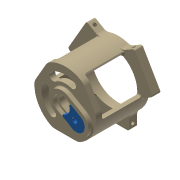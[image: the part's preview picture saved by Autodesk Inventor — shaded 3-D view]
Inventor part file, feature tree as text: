
AUTODESK INVENTOR PART (.ipt)
format: ipt  version: 2015 (Build 190159000, 159)  size: 2,890,752 bytes
history: native  units: in
note: dims shown in document units (in); Inventor stores cm internally (conversion verified against a paired STEP export)
features: extrude x13, sketch x11, fillet x8, other x6, projected_geometry x5, pattern_circular x4, plane x3, mirror x1
ambient origin geometry x8: Origin, YZ Plane, XZ Plane, XY Plane, X Axis, Y Axis, Z Axis, Center Point
bodies: Body1 (feature_tree), Body2 (feature_tree), Body3 (feature_tree), Body4 (feature_tree), Body5 (feature_tree), Body6 (feature_tree), Body7 (feature_tree), Body8 (feature_tree), Body9 (feature_tree), Body10 (feature_tree), Body11 (feature_tree), Body12 (feature_tree), Body13 (feature_tree), Body14 (feature_tree), Body15 (feature_tree), Body16 (feature_tree), Body17 (feature_tree), Body18 (feature_tree), Body19 (feature_tree), Body20 (feature_tree), Body21 (feature_tree), Body22 (feature_tree), Body23 (feature_tree), Body24 (feature_tree), Body25 (feature_tree), Body26 (feature_tree), Body27 (feature_tree), Body28 (feature_tree), Body29 (feature_tree), Body30 (feature_tree), Body31 (feature_tree), Body32 (feature_tree), Body33 (feature_tree), Body34 (feature_tree), Body35 (feature_tree), Body36 (feature_tree), Body37 (feature_tree), Body38 (feature_tree), Body39 (feature_tree), Body40 (feature_tree), Body41 (feature_tree), Body42 (feature_tree), Body43 (feature_tree), Body44 (feature_tree), Body45 (feature_tree), Body46 (feature_tree), Body47 (feature_tree), Body48 (feature_tree), Body49 (feature_tree), Body50 (feature_tree), Body51 (feature_tree), Body52 (feature_tree), Body53 (feature_tree), Body54 (feature_tree), Body55 (feature_tree), Body56 (feature_tree), Body57 (feature_tree), Body58 (feature_tree), Body59 (feature_tree), Body60 (feature_tree), Body61 (feature_tree), Body62 (feature_tree), Body63 (feature_tree), Body64 (feature_tree), Body65 (feature_tree), Body66 (feature_tree), Body67 (feature_tree), Body68 (feature_tree), Body69 (feature_tree), Body70 (feature_tree), Body71 (feature_tree), Body72 (feature_tree), Body73 (feature_tree), Body74 (feature_tree), Body75 (feature_tree), Body76 (feature_tree), Body77 (feature_tree), Body78 (feature_tree), Body79 (feature_tree), Body80 (feature_tree), Body81 (feature_tree), Body82 (feature_tree), Body83 (feature_tree), Body84 (feature_tree), Body85 (feature_tree), Body86 (feature_tree), Body87 (feature_tree), Body88 (feature_tree), Body89 (feature_tree), Body90 (feature_tree), Body91 (feature_tree), Body92 (feature_tree), Body93 (feature_tree), Body94 (feature_tree), Body95 (feature_tree), Body96 (feature_tree), Body97 (feature_tree), Body98 (feature_tree), Body99 (feature_tree), Body100 (feature_tree), Body101 (feature_tree), Body102 (feature_tree), Body103 (feature_tree), Body104 (feature_tree), Body105 (feature_tree), Body106 (feature_tree), Body107 (feature_tree), Body108 (feature_tree), Body109 (feature_tree), Body110 (feature_tree), Body111 (feature_tree), Body112 (feature_tree), Body113 (feature_tree), Body114 (feature_tree), Body115 (feature_tree), Body116 (feature_tree), Body117 (feature_tree), Body118 (feature_tree), Body119 (feature_tree), Body120 (feature_tree), Body121 (feature_tree), Body122 (feature_tree), Body123 (feature_tree), Body124 (feature_tree), Body125 (feature_tree), Body126 (feature_tree), Body127 (feature_tree), Body128 (feature_tree), Body129 (feature_tree), Body130 (feature_tree), Body131 (feature_tree), Body132 (feature_tree), Body133 (feature_tree), Body134 (feature_tree), Body135 (feature_tree), Body136 (feature_tree), Body137 (feature_tree), Body138 (feature_tree), Body139 (feature_tree), Body140 (feature_tree), Body141 (feature_tree), Body142 (feature_tree), Body143 (feature_tree), Body144 (feature_tree), Body145 (feature_tree), Body146 (feature_tree), Body147 (feature_tree), Body148 (feature_tree), Body149 (feature_tree), Body150 (feature_tree), Body151 (feature_tree), Body152 (feature_tree), Body153 (feature_tree), Body154 (feature_tree), Body155 (feature_tree), Body156 (feature_tree), Body157 (feature_tree), Body158 (feature_tree), Body159 (feature_tree), Body160 (feature_tree), Body161 (feature_tree), Body162 (feature_tree), Body163 (feature_tree), Body164 (feature_tree), Body165 (feature_tree), Body166 (feature_tree), Body167 (feature_tree), Body168 (feature_tree), Body169 (feature_tree), Body170 (feature_tree), Body171 (feature_tree), Body172 (feature_tree), Body173 (feature_tree), Body174 (feature_tree), Body175 (feature_tree), Body176 (feature_tree), Body177 (feature_tree), Body178 (feature_tree), Body179 (feature_tree), Body180 (feature_tree), Body181 (feature_tree), Body182 (feature_tree), Body183 (feature_tree), Body184 (feature_tree), Body185 (feature_tree), Body186 (feature_tree), Body187 (feature_tree), Body188 (feature_tree), Body189 (feature_tree), Body190 (feature_tree), Body191 (feature_tree), Body192 (feature_tree), Body193 (feature_tree), Body194 (feature_tree), Body195 (feature_tree), Body196 (feature_tree), Body197 (feature_tree), Body198 (feature_tree), Body199 (feature_tree), Body200 (feature_tree), Body201 (feature_tree), Body202 (feature_tree), Body203 (feature_tree), Body204 (feature_tree), Body205 (feature_tree), Body206 (feature_tree), Body207 (feature_tree), Body208 (feature_tree), Body209 (feature_tree), Body210 (feature_tree), Body211 (feature_tree), Body212 (feature_tree), Body213 (feature_tree), Body214 (feature_tree), Body215 (feature_tree), Body216 (feature_tree), Body217 (feature_tree), Body218 (feature_tree), Body219 (feature_tree), Body220 (feature_tree), Body221 (feature_tree), Body222 (feature_tree), Body223 (feature_tree), Body224 (feature_tree), Body225 (feature_tree), Body226 (feature_tree), Body227 (feature_tree), Body228 (feature_tree), Body229 (feature_tree), Body230 (feature_tree), Body231 (feature_tree), Body232 (feature_tree), Body233 (feature_tree), Body234 (feature_tree), Body235 (feature_tree), Body236 (feature_tree), Body237 (feature_tree), Body238 (feature_tree), Body239 (feature_tree), Body240 (feature_tree), Body241 (feature_tree), Body242 (feature_tree), Body243 (feature_tree), Body244 (feature_tree), Body245 (feature_tree), Body246 (feature_tree), Body247 (feature_tree), Body248 (feature_tree), Body249 (feature_tree), Body250 (feature_tree), Body251 (feature_tree), Body252 (feature_tree), Body253 (feature_tree), Body254 (feature_tree), Body255 (feature_tree), Body256 (feature_tree), Body257 (feature_tree), Body258 (feature_tree), Body259 (feature_tree), Body260 (feature_tree), Body261 (feature_tree), Body262 (feature_tree), Body263 (feature_tree), Body264 (feature_tree), Body265 (feature_tree), Body266 (feature_tree), Body267 (feature_tree), Body268 (feature_tree), Body269 (feature_tree), Body270 (feature_tree), Body271 (feature_tree), Body272 (feature_tree), Body273 (feature_tree), Body274 (feature_tree), Body275 (feature_tree), Body276 (feature_tree), Body277 (feature_tree), Body278 (feature_tree), Body279 (feature_tree), Body280 (feature_tree), Body281 (feature_tree), Body282 (feature_tree), Body283 (feature_tree), Body284 (feature_tree), Body285 (feature_tree), Body286 (feature_tree), Body287 (feature_tree), Body288 (feature_tree), Body289 (feature_tree), Body290 (feature_tree), Body291 (feature_tree), Body292 (feature_tree), Body293 (feature_tree), Body294 (feature_tree), Body295 (feature_tree), Body296 (feature_tree), Body297 (feature_tree), Body298 (feature_tree), Body299 (feature_tree), Body300 (feature_tree), Body301 (feature_tree), Body302 (feature_tree), Body303 (feature_tree), Body304 (feature_tree), Body305 (feature_tree), Body306 (feature_tree), Body307 (feature_tree), Body308 (feature_tree), Body309 (feature_tree), Body310 (feature_tree), Body311 (feature_tree), Body312 (feature_tree), Body313 (feature_tree), Body314 (feature_tree), Body315 (feature_tree), Body316 (feature_tree), Body317 (feature_tree), Body318 (feature_tree), Body319 (feature_tree), Body320 (feature_tree), Body321 (feature_tree), Body322 (feature_tree), Body323 (feature_tree), Body324 (feature_tree), Body325 (feature_tree), Body326 (feature_tree), Body327 (feature_tree), Body328 (feature_tree), Body329 (feature_tree), Body330 (feature_tree), Body331 (feature_tree), Body332 (feature_tree), Body333 (feature_tree), Body334 (feature_tree), Body335 (feature_tree), Body336 (feature_tree), Body337 (feature_tree), Body338 (feature_tree), Body339 (feature_tree), Body340 (feature_tree), Body341 (feature_tree), Body342 (feature_tree), Body343 (feature_tree), Body344 (feature_tree), Body345 (feature_tree), Body346 (feature_tree), Body347 (feature_tree), Body348 (feature_tree), Body349 (feature_tree), Body350 (feature_tree), Body351 (feature_tree), Body352 (feature_tree), Body353 (feature_tree), Body354 (feature_tree), Body355 (feature_tree), Body356 (feature_tree), Body357 (feature_tree), Body358 (feature_tree), Body359 (feature_tree), Body360 (feature_tree), Body361 (feature_tree), Body362 (feature_tree), Body363 (feature_tree), Body364 (feature_tree), Body365 (feature_tree), Body366 (feature_tree), Body367 (feature_tree), Body368 (feature_tree), Body369 (feature_tree), Body370 (feature_tree), Body371 (feature_tree), Body372 (feature_tree), Body373 (feature_tree), Body374 (feature_tree), Body375 (feature_tree), Body376 (feature_tree), Body377 (feature_tree), Body378 (feature_tree), Body379 (feature_tree), Body380 (feature_tree), Body381 (feature_tree), Body382 (feature_tree), Body383 (feature_tree), Body384 (feature_tree), Body385 (feature_tree), Body386 (feature_tree), Body387 (feature_tree), Body388 (feature_tree), Body389 (feature_tree), Body390 (feature_tree), Body391 (feature_tree), Body392 (feature_tree), Body393 (feature_tree), Body394 (feature_tree), Body395 (feature_tree), Body396 (feature_tree), Body397 (feature_tree), Body398 (feature_tree), Body399 (feature_tree), Body400 (feature_tree), Body401 (feature_tree), Body402 (feature_tree), Body403 (feature_tree), Body404 (feature_tree), Body405 (feature_tree), Body406 (feature_tree), Body407 (feature_tree), Body408 (feature_tree), Body409 (feature_tree), Body410 (feature_tree), Body411 (feature_tree), Body412 (feature_tree), Body413 (feature_tree), Body414 (feature_tree), Body415 (feature_tree), Body416 (feature_tree), Body417 (feature_tree), Body418 (feature_tree), Body419 (feature_tree), Body420 (feature_tree), Body421 (feature_tree), Body422 (feature_tree), Body423 (feature_tree), Body424 (feature_tree), Body425 (feature_tree), Body426 (feature_tree), Body427 (feature_tree), Body428 (feature_tree), Body429 (feature_tree), Body430 (feature_tree), Body431 (feature_tree), Body432 (feature_tree), Body433 (feature_tree), Body434 (feature_tree), Body435 (feature_tree), Body436 (feature_tree), Body437 (feature_tree), Body438 (feature_tree), Body439 (feature_tree), Body440 (feature_tree), Body441 (feature_tree), Body442 (feature_tree), Body443 (feature_tree), Body444 (feature_tree), Body445 (feature_tree), Body446 (feature_tree), Body447 (feature_tree), Body448 (feature_tree), Body449 (feature_tree), Body450 (feature_tree), Body451 (feature_tree), Body452 (feature_tree), Body453 (feature_tree), Body454 (feature_tree), Body455 (feature_tree), Body456 (feature_tree), Body457 (feature_tree), Body458 (feature_tree), Body459 (feature_tree), Body460 (feature_tree), Body461 (feature_tree), Body462 (feature_tree), Body463 (feature_tree), Body464 (feature_tree), Body465 (feature_tree), Body466 (feature_tree), Body467 (feature_tree), Body468 (feature_tree), Body469 (feature_tree), Body470 (feature_tree), Body471 (feature_tree), Body472 (feature_tree), Body473 (feature_tree), Body474 (feature_tree), Body475 (feature_tree), Body476 (feature_tree), Body477 (feature_tree), Body478 (feature_tree), Body479 (feature_tree), Body480 (feature_tree), Body481 (feature_tree), Body482 (feature_tree), Body483 (feature_tree), Body484 (feature_tree), Body485 (feature_tree), Body486 (feature_tree), Body487 (feature_tree), Body488 (feature_tree), Body489 (feature_tree), Body490 (feature_tree), Body491 (feature_tree), Body492 (feature_tree), Body493 (feature_tree), Body494 (feature_tree), Body495 (feature_tree), Body496 (feature_tree), Body497 (feature_tree), Body498 (feature_tree)
feature tree (51):
  other  "Hat"
  other  "68304 platform1"
  extrude  "Extrusion1"  Depth=0.1575in TaperAngle=0.0deg
  extrude  "Extrusion2"  Depth=1.1811in TaperAngle=0.0deg
  pattern_circular  "Circular Pattern1"  Count=3 Angle=360.0deg
  plane  "Work Plane1"
  extrude  "Extrusion3"  Depth=0.1718in
  pattern_circular  "Circular Pattern2"  Count=3 Angle=360.0deg
  extrude  "Extrusion4"  Depth=0.2264in TaperAngle=0.0deg
  extrude  "Extrusion5"  Depth=1.1811in TaperAngle=0.0deg
  pattern_circular  "Circular Pattern3"  Count=3 Angle=360.0deg
  extrude  "Extrusion6"  Depth=0.8976in
  extrude  "Extrusion11"  Depth=0.1575in
  fillet  "Fillet1"  Radius=0.2343in
  fillet  "Fillet2"  Radius=0.6398in
  fillet  "Fillet4"  Radius=0.1575in
  fillet  "Fillet5"  Radius=0.1575in
  extrude  "Extrusion8"  Depth=0.0787in
  plane  "Work Plane2"
  mirror  "Mirror1"
  other  "Work Axis1"
  plane  "Work Plane3"
  extrude  "Extrusion9"  Depth=0.3937in
  pattern_circular  "Circular Pattern4"  [2 undecoded]
  fillet  "Fillet6"  Radius=0.1969in
  extrude  "Extrusion12"  Depth=0.3937in
  extrude  "Extrusion13"  Depth=0.3937in
  fillet  "Fillet9"  [1 undecoded]
  fillet  "Fillet10"  Radius=0.3951in
  fillet  "Fillet11"  Radius=0.1467in
  extrude  "Extrusion14"  Depth=0.3937in
  extrude  "Extrusion15"  Depth=0.3937in TaperAngle=0.0deg
  sketch  "Sketch1"  dims[d0=0.1575in d1=0.315in d2=0.0in]
  sketch  "Sketch2"  dims[d3=0.13in d4=0.315in d5=0.0in d6=1.1811in d7=360.0deg]
  sketch  "Sketch3"  dims[d9=1.5354in d10=0.1718in]
  sketch  "Sketch4"  dims[d11=0.1718in]
  sketch  "Sketch5"  dims[d12=60.0deg]
  sketch  "Sketch6"  dims[d13=0.315in d14=0.0in d15=1.1811in d16=360.0deg]
  sketch  "Sketch7"  dims[d18=0.4823in d19=0.2264in d20=0.0in]
  sketch  "Sketch8"  dims[d21=0.3937in d22=0.2343in d23=0.0in d24=1.1811in d25=360.0deg]
  sketch  "Sketch9"  dims[d27=0.6496in d28=0.8976in]
  projected_geometry  "Projected Loop1"
  projected_geometry  "Projected Loop2"
  other  "Plug"
  projected_geometry  "Projected Loop3"
  sketch  "Sketch14"  dims[d29=60.0deg d30=0.5906in d31=0.2343in d32=0.0in d33=0.6398in d34=0.2411in d35=0.1575in d36=0.1575in]
  projected_geometry  "Projected Loop4"
  projected_geometry  "Projected Loop5"
  sketch  "Sketch16"  dims[d37=0.3199in d40=0.0787in d41=0.3937in d43=0.0394in d44=0.1969in d45=0.1181in d46=0.1181in d47=22.5deg d48=0.3951in d49=0.1467in d50=0.0in d51=0.0394in d52=0.1467in d53=0.0in d54=0.0in d58=1.1811in d59=360.0deg d65=0.0787in d66=0.1467in d67=0.0in d68=0.0197in d69=0.0394in d70=0.0039in d71=0.0039in d72=0.1181in d73=0.1969in d74=0.1467in d75=0.0in d76=0.0039in d77=0.0039in d78=0.0039in d79=0.0039in d80=0.0039in d81=0.0039in d82=0.0039in d83=0.0039in d84=0.0039in d85=0.0039in d86=0.0039in d87=0.1467in d88=0.0in d91=0.4823in d92=0.0394in d93=0.0197in d94=0.0787in d95=0.0984in d96=0.3937in d97=0.0in d98=0.1969in d99=0.3937in d100=0.0in]
  other  "Composite1"
  other  "Srf1"
note: 3 required parameter values undecoded (feature->parameter linkage not recoverable at this tier; creation-order binding heuristic only, values carry confidence <= 0.55)
